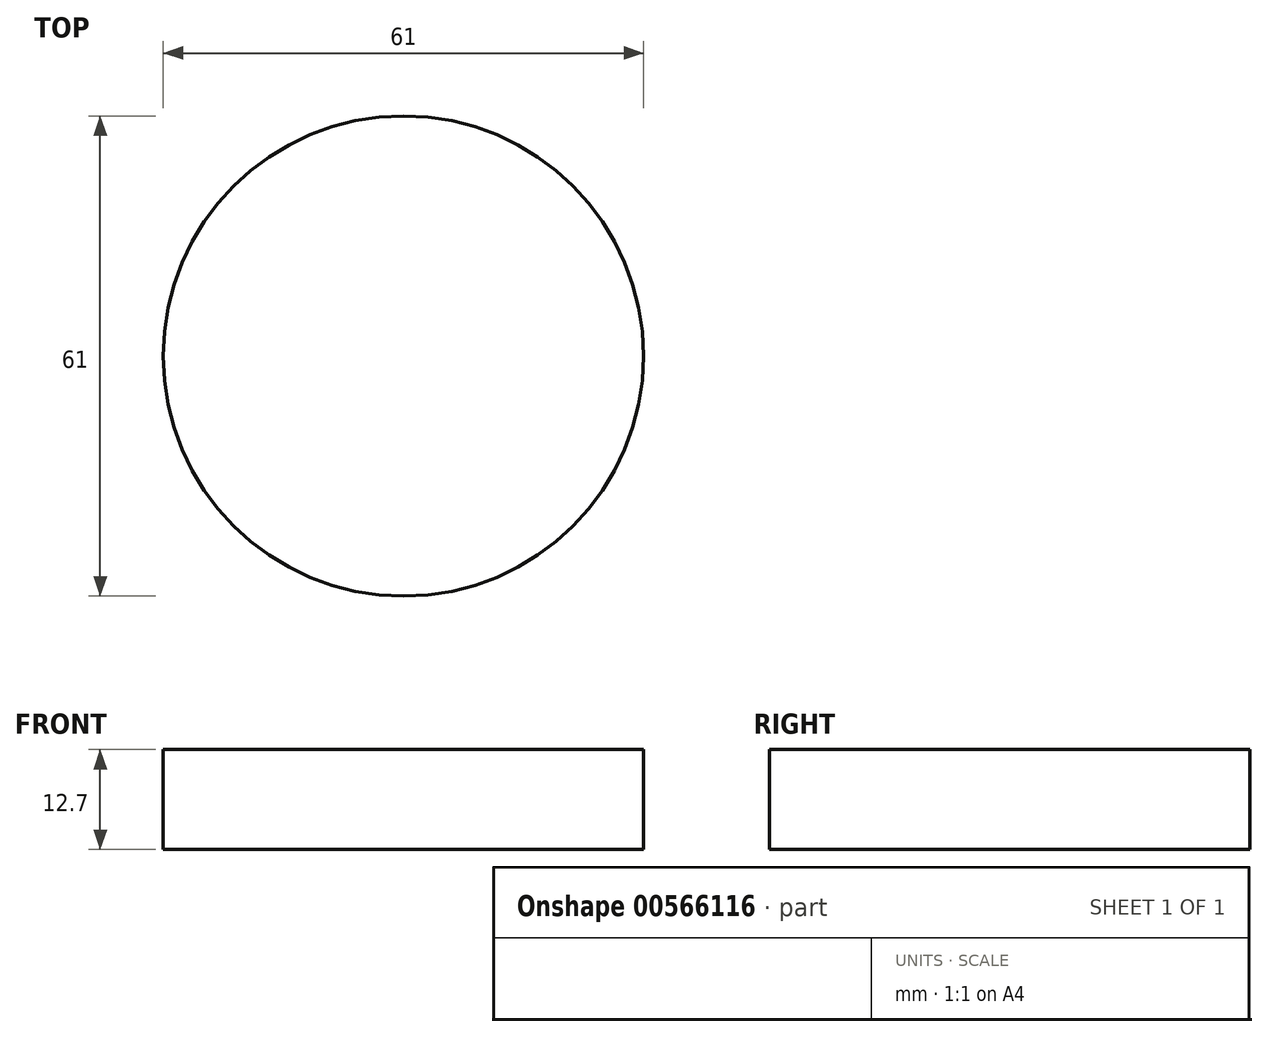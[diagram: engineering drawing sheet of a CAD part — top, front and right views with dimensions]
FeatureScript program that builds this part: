
annotation { "Feature Type Name" : "Feature", "Feature Type Description" : "" }
export const myFeature = defineFeature(function(context is Context, id is Id, definition is map)
    precondition{}
    {
        {
            var Q0;
            Q0=qCreatedBy(makeId("Top.planeOp"),FACE);
            var sketch = newSketch(context, id + "F0", { "sketchPlane" : qUnion([Q0])});
            skCircle(sketch, "E0", {"center": v(0, 0) * mm, "radius": 30.5 * mm});
            skSolve(sketch);
        }
        {
            var Q0;
            Q0 = qSketchRegion(id + "F0", true);
            extrude(context, id + "F1", {"entities" : qUnion([Q0]), "depth" : 12.7 * mm, "offsetDistance" : 25.4 * mm});
        }
    });
